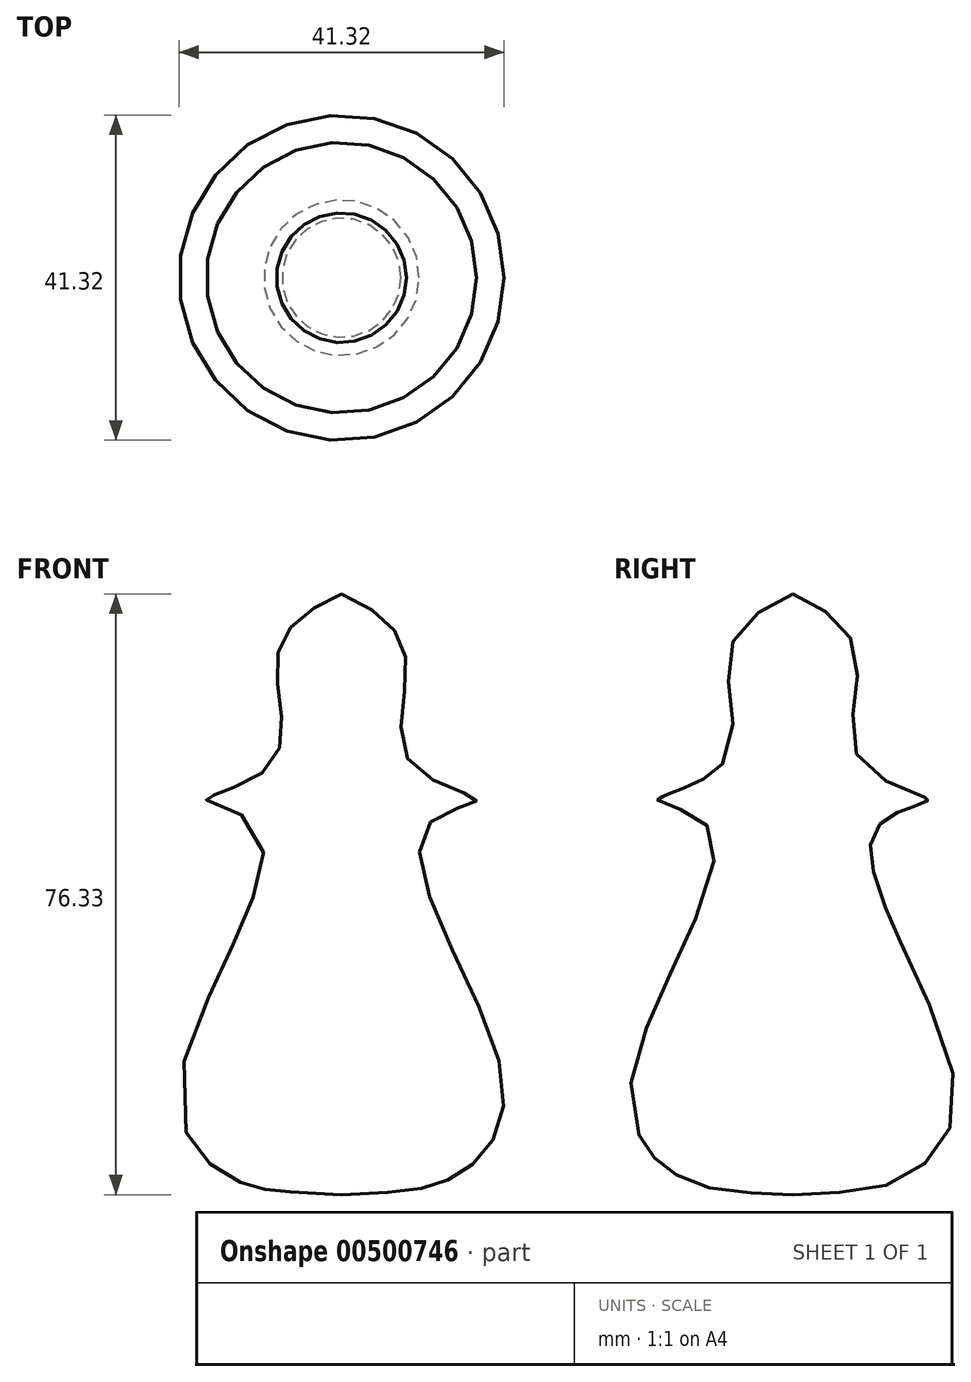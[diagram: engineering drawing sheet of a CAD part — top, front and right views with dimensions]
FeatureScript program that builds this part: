
annotation { "Feature Type Name" : "Feature", "Feature Type Description" : "" }
export const myFeature = defineFeature(function(context is Context, id is Id, definition is map)
    precondition{}
    {
        {
            var Q0;
            Q0=qCreatedBy(makeId("Front.planeOp"),FACE);
            var sketch = newSketch(context, id + "F0", { "sketchPlane" : qUnion([Q0])});
            skLineSegment(sketch, "E0", {"start": v(0, 0) * mm, "end": v(0, 76.33) * mm});
            skFitSpline(sketch, "E1", {"points": [v(0, 76.33) * mm, v(8.13, 68.47) * mm, v(8.82, 54.8) * mm, v(17.17, 50.1) * mm, v(10.43, 46.26) * mm, v(20.51, 14.48) * mm, v(14.76, 2.5) * mm, v(0, 0) * mm], "startDerivative": vector(96.8, -43.6) * mm, "endDerivative": vector(-157.73, -6.63) * mm});
            skSolve(sketch);
        }
        {
            var Q0;
            Q0=makeQuery(id+"F0.imprint","IMPRINT",FACE,{"disambiguationData":[TD([[makeQuery(id+"F0.imprint","IMPRINT",EDGE,{"derivedFrom":sQuery(id+"F0.wireOp",EDGE,"E0")}),-1.0]])]});
            var Q1;
            Q1=sQuery(id+"F0.wireOp",EDGE,"E0");
            revolve(context, id + "F1", {"entities" : qUnion([Q0]), "axis" : qUnion([Q1]), "revolveType" : RevolveType.FULL});
        }
    });
